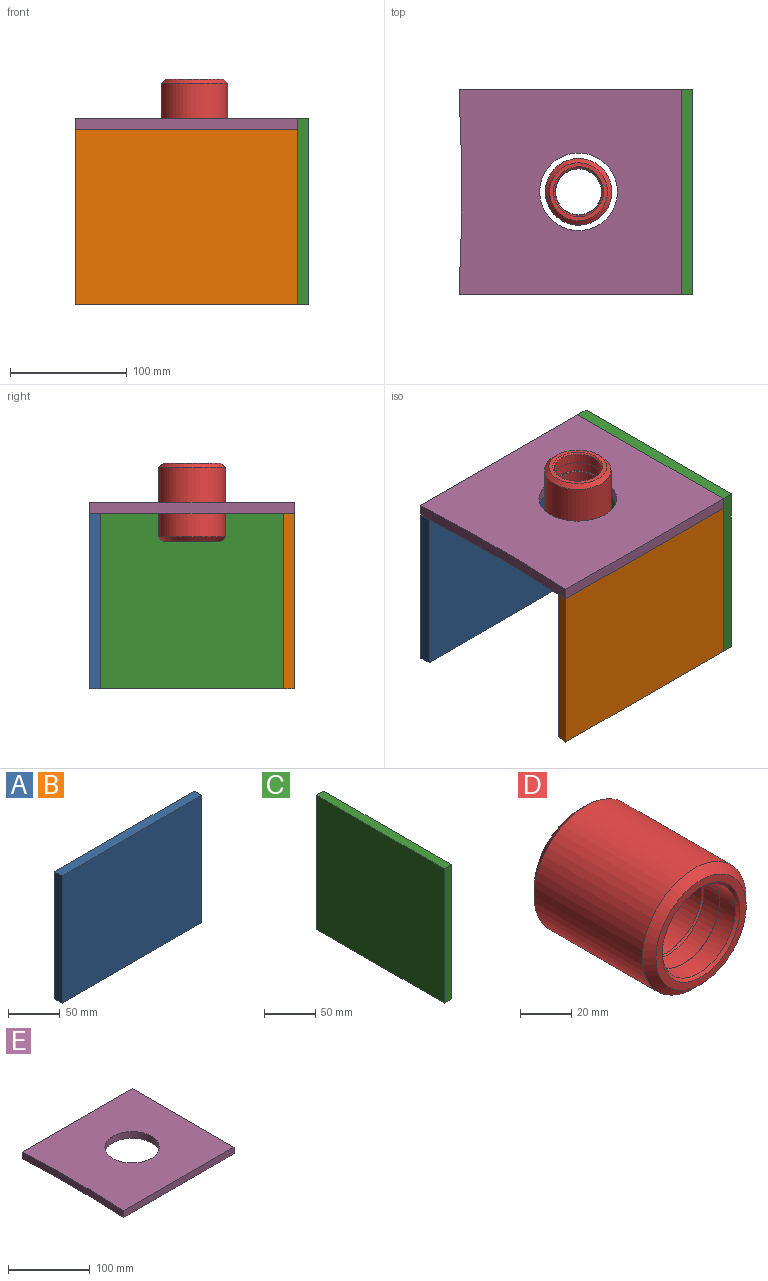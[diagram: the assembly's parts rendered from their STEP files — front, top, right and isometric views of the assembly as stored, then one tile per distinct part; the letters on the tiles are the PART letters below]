
ASSEMBLY  parts=5 mates=4
PART A: 6 faces, bbox 190.3x10x150 mm
  f0: cylinder r=1665mm len=150mm, axis (0,0,-1), area 1501.9mm2, adj f1,f3,f4,f5
  f1: plane 189.83x150mm, normal (0,-1,0), area 28474.2mm2, adj f0,f2,f4,f5
  f2: plane 150x10mm, normal (1,0,0), area 1500mm2, adj f1,f3,f4,f5
  f3: plane 190.33x150mm, normal (0,1,0), area 28549.1mm2, adj f0,f2,f4,f5
  f4: plane 190.33x10mm, normal (0,0,1), area 1900.7mm2, adj f0,f1,f2,f3
  f5: plane 190.33x10mm, normal (0,0,-1), area 1900.7mm2, adj f0,f1,f2,f3
PART B: same geometry as A
PART C: 6 faces, bbox 10x176x160 mm
  f0: plane 160x10mm, normal (0,-1,0), area 1600mm2, adj f1,f3,f4,f5
  f1: plane 176x10mm, normal (0,0,-1), area 1760mm2, adj f0,f2,f4,f5
  f2: plane 160x10mm, normal (0,1,0), area 1600mm2, adj f1,f3,f4,f5
  f3: plane 176x10mm, normal (0,0,1), area 1760mm2, adj f0,f2,f4,f5
  f4: plane 176x160mm, normal (1,0,0), area 28160mm2, adj f0,f1,f2,f3
  f5: plane 176x160mm, normal (-1,0,0), area 28160mm2, adj f0,f1,f2,f3
PART D: 24 faces, bbox 57x67x57 mm
  f0: plane 49.58x49.58mm, normal (0,1,0), area 494mm2, adj f1,f23
  f1: revolved ~57x57mm, area 878.2mm2, adj f0,f2
  f2: revolved ~59.58x57mm, area 10669.4mm2, adj f1,f3
  f3: revolved ~57x57mm, area 1756.3mm2, adj f2,f4
  f4: plane 49.58x49.58mm, normal (0,-1,0), area 494mm2, adj f3,f5
  f5: revolved ~42.77x42.77mm, area 224.1mm2, adj f4,f7
  f6: revolved ~39.77x39.77mm, area 1027.7mm2, adj f8,f11
  f7: revolved ~40.31x40.31mm, area 2144.3mm2, adj f5,f10
  f8: plane 42.16x42.16mm, normal (0,-1,0), area 153.9mm2, adj f6,f9
  f9: revolved ~42.16x42.16mm, area 1.4mm2, adj f8,f10
  f10: plane 42.16x42.16mm, normal (0,1,0), area 153.8mm2, adj f7,f9
  f11: plane 41.72x41.72mm, normal (0,1,0), area 156.8mm2, adj f6,f12
  f12: revolved ~41.72x41.72mm, area 215.3mm2, adj f11,f13
  f13: plane 39.33x39.33mm, normal (0,-1,0), area 4.6mm2, adj f12,f14
  f14: revolved ~39.26x39.26mm, area 3528.2mm2, adj f13,f15
  f15: plane 39.33x39.33mm, normal (0,1,0), area 4.6mm2, adj f14,f16
  f16: revolved ~41.72x41.72mm, area 215.3mm2, adj f15,f17
  f17: plane 41.72x41.72mm, normal (0,-1,0), area 156.8mm2, adj f16,f18
  f18: revolved ~39.77x39.77mm, area 1027.7mm2, adj f17,f20
  f19: revolved ~40.31x40.31mm, area 1072.2mm2, adj f22,f23
  f20: plane 42.16x42.16mm, normal (0,1,0), area 153.9mm2, adj f18,f21
  f21: revolved ~42.16x42.16mm, area 1.3mm2, adj f20,f22
  f22: plane 42.16x42.16mm, normal (0,-1,0), area 153.8mm2, adj f19,f21
  f23: revolved ~42.77x42.77mm, area 224.1mm2, adj f0,f19
PART E: 7 faces, bbox 190.3x176x10 mm
  f0: cylinder r=1665mm len=176mm, axis (0,0,-1), area 1760.8mm2, adj f1,f3,f5,f6
  f1: plane 190.33x10mm, normal (0,-1,0), area 1903.3mm2, adj f0,f2,f5,f6
  f2: plane 176x10mm, normal (1,0,0), area 1760mm2, adj f1,f3,f5,f6
  f3: plane 190.33x10mm, normal (0,1,0), area 1903.3mm2, adj f0,f2,f5,f6
  f4: cylinder r=33.25mm len=66.5mm, axis (0,0,-1), area 2089.2mm2, adj f5,f6
  f5: plane 190.33x176mm, normal (0,0,1), area 29751.3mm2, adj f0,f1,f2,f3,f4
  f6: plane 190.33x176mm, normal (0,0,-1), area 29751.3mm2, adj f0,f1,f2,f3,f4
PLACE A t=(-1008.64,76.84,-371.31)mm
PLACE B rot(axis=(1,0,0),180deg) t=(-1008.64,76.84,-221.31)mm
PLACE C t=(-1008.64,76.84,-371.31)mm
PLACE D rot(axis=(1,0,0),90deg) t=(756.36,76.84,-244.81)mm
PLACE E t=(-1008.64,76.84,-371.31)mm
MATE fastened B.f3 <-> E.f1  axis (0,-1,0) through (844.36,-11.16,-221.31)mm
MATE fastened A.f3 <-> E.f3  axis (0,1,0) through (844.36,164.84,-221.31)mm
MATE fastened C.f3 <-> E.f5  axis (0,0,1) through (844.36,76.84,-211.31)mm
MATE fastened D.f1 <-> E.f4  axis (0,0,1) through (756.36,76.84,-211.31)mm
